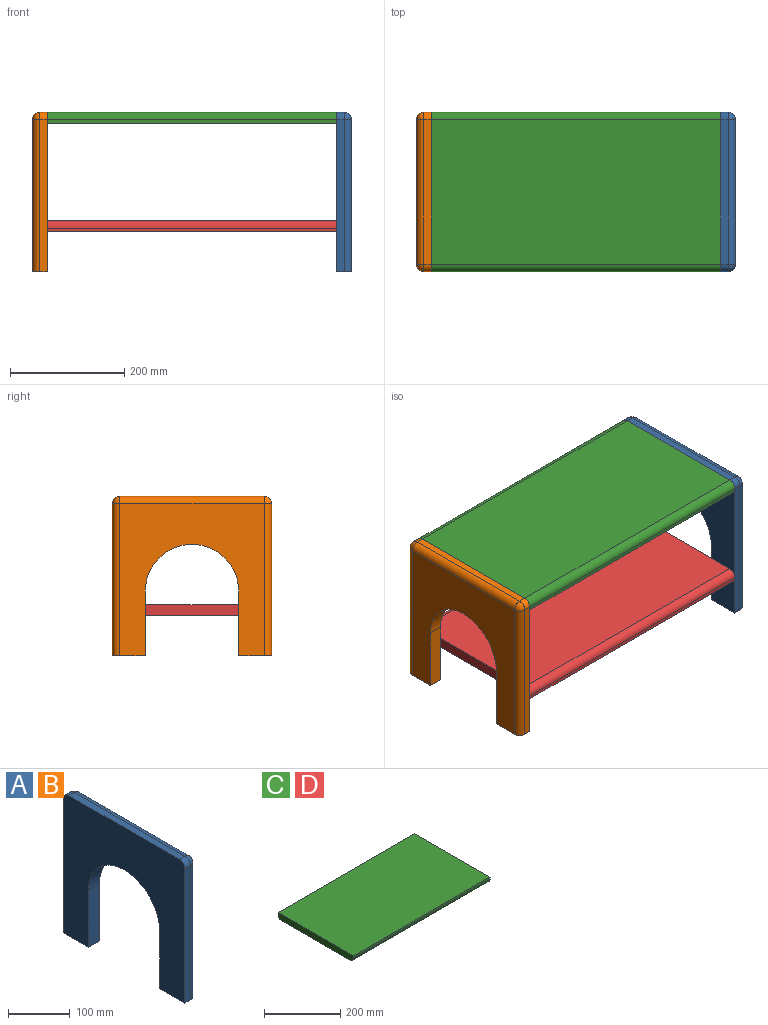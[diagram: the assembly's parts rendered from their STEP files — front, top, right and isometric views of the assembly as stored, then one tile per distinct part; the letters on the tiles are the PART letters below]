
ASSEMBLY  parts=4 mates=6
PART A: 17 faces, bbox 25.4x279.4x279.4 mm
  f0: plane 57.76x25.4mm, normal (0,0,-1), area 1432.5mm2, adj f1,f2,f5,f7,f12
  f1: plane 266.7x254mm, normal (1,0,0), area 38632.6mm2, adj f0,f4,f7,f8,f9,f12,f14,f16
  f2: plane 279.4x279.4mm, normal (-1,0,0), area 48885.9mm2, adj f0,f3,f4,f5,f6,f7,f8,f9
  f3: plane 266.7x12.7mm, normal (0,-1,0), area 3387.1mm2, adj f2,f4,f11,f16
  f4: plane 57.76x25.4mm, normal (0,0,-1), area 1432.5mm2, adj f1,f2,f3,f8,f16
  f5: plane 266.7x12.7mm, normal (0,1,0), area 3387.1mm2, adj f0,f2,f10,f12
  f6: plane 254x12.7mm, normal (0,0,1), area 3225.8mm2, adj f2,f10,f11,f14
  f7: plane 113.27x25.4mm, normal (0,-1,0), area 2876.9mm2, adj f0,f1,f2,f9
  f8: plane 113.27x25.4mm, normal (0,1,0), area 2876.9mm2, adj f1,f2,f4,f9
  f9: cylinder r=81.94mm len=163.88mm, axis (1,0,0), area 6538.6mm2, adj f1,f2,f7,f8
  f10: cylinder r=12.7mm len=12.7mm, axis (1,0,0), area 253.4mm2, adj f2,f5,f6,f13
  f11: cylinder r=12.7mm len=12.7mm, axis (-1,0,0), area 253.4mm2, adj f2,f3,f6,f15
  f12: cylinder r=12.7mm len=266.7mm, axis (0,0,-1), area 5320.4mm2, adj f0,f1,f5,f13
  f13: sphere r=12.7mm, area 253.4mm2, adj f10,f12,f14
  f14: cylinder r=12.7mm len=254mm, axis (0,1,0), area 5067.1mm2, adj f1,f6,f13,f15
  f15: sphere r=12.7mm, area 253.4mm2, adj f11,f14,f16
  f16: cylinder r=12.7mm len=266.7mm, axis (0,0,1), area 5320.4mm2, adj f1,f3,f4,f15
PART B: same geometry as A
PART C: 8 faces, bbox 508x279.4x19.1 mm
  f0: plane 508x6.35mm, normal (0,1,0), area 3225.8mm2, adj f1,f3,f4,f7
  f1: plane 279.4x19.05mm, normal (-1,0,0), area 5253.3mm2, adj f0,f2,f4,f5,f6,f7
  f2: plane 508x6.35mm, normal (0,-1,0), area 3225.8mm2, adj f1,f3,f4,f6
  f3: plane 279.4x19.05mm, normal (1,0,0), area 5253.3mm2, adj f0,f2,f4,f5,f6,f7
  f4: plane 508x279.4mm, normal (0,0,1), area 141935.2mm2, adj f0,f1,f2,f3
  f5: plane 508x254mm, normal (0,0,-1), area 129032mm2, adj f1,f3,f6,f7
  f6: cylinder r=12.7mm len=508mm, axis (1,0,0), area 10134.1mm2, adj f1,f2,f3,f5
  f7: cylinder r=12.7mm len=508mm, axis (-1,0,0), area 10134.1mm2, adj f0,f1,f3,f5
PART D: same geometry as C
PLACE A t=(-25.4,690.98,-249.96)mm
PLACE B rot(axis=(0,0,1),180deg) t=(-533.4,970.38,-249.96)mm
PLACE C rot(axis=(0,-1,0),180deg) t=(-533.4,690.98,29.44)mm
PLACE D rot(axis=(0,1,0),180deg) t=(-533.4,690.98,-161.06)mm
MATE planar D.f2 <-> A.f3  axis (0,-1,0) through (-279.4,690.98,-176.94)mm
MATE planar C.f3 <-> B.f2  axis (-1,0,0) through (-533.4,830.68,19.82)mm
MATE planar A.f6 <-> C.f5  axis (0,0,1) through (-19.05,830.68,29.44)mm
MATE planar A.f2 <-> C.f1  axis (-1,0,0) through (-25.4,830.68,-80.71)mm
MATE planar A.f2 <-> D.f1  axis (-1,0,0) through (-25.4,830.68,-80.71)mm
MATE planar B.f6 <-> C.f5  axis (0,0,1) through (-539.75,830.68,29.44)mm
